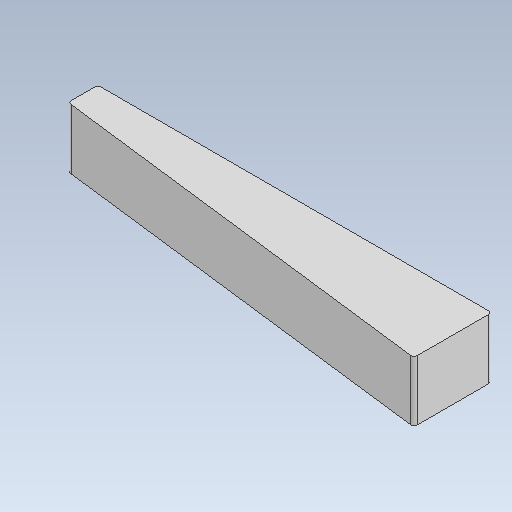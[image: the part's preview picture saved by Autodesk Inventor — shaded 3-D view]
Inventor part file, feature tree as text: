
AUTODESK INVENTOR PART (.ipt)
format: ipt  version: 2020 (Build 240168000, 168)  size: 96,256 bytes
history: native  units: mm
features: extrude x1, sketch x1
ambient origin geometry x8: Origin, YZ Plane, XZ Plane, XY Plane, X Axis, Y Axis, Z Axis, Center Point
bodies: Solid1 (feature_tree)
feature tree (2):
  extrude  "Extrusion1"  Depth=39.333333mm
  sketch  "Sketch1"  dims[d0=38.666667mm d1=0.666667mm d2=0.666667mm d4=0.666667mm d5=2.666667mm d6=1.22173mm d7=0.666667mm d8=6.0mm d9=0.0mm d11=39.333333mm]
